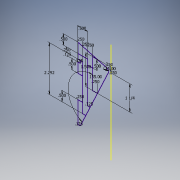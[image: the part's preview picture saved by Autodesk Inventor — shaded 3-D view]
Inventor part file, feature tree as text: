
AUTODESK INVENTOR PART (.ipt)
format: ipt  version: 2017 (Build 210142000, 142)  size: 116,736 bytes
history: native  units: in
note: dims shown in document units (in); Inventor stores cm internally (conversion verified against a paired STEP export)
features: sketch x1
ambient origin geometry x8: Origin, YZ Plane, XZ Plane, XY Plane, X Axis, Y Axis, Z Axis, Center Point
feature tree (1):
  sketch  "Sketch1"  dims[d0=0.25in d1=0.1718in d2=15.0deg d4=0.25in d5=1.5in d6=1.25in d7=0.25in d11=0.25in d13=0.5in d15=0.25in d16=0.25in d18=0.125in d19=0.5in d20=0.125in d21=0.25in d22=0.125in d23=0.125in d24=0.25in d25=0.5in d26=2.292in d27=0.5in d29=0.5in]
